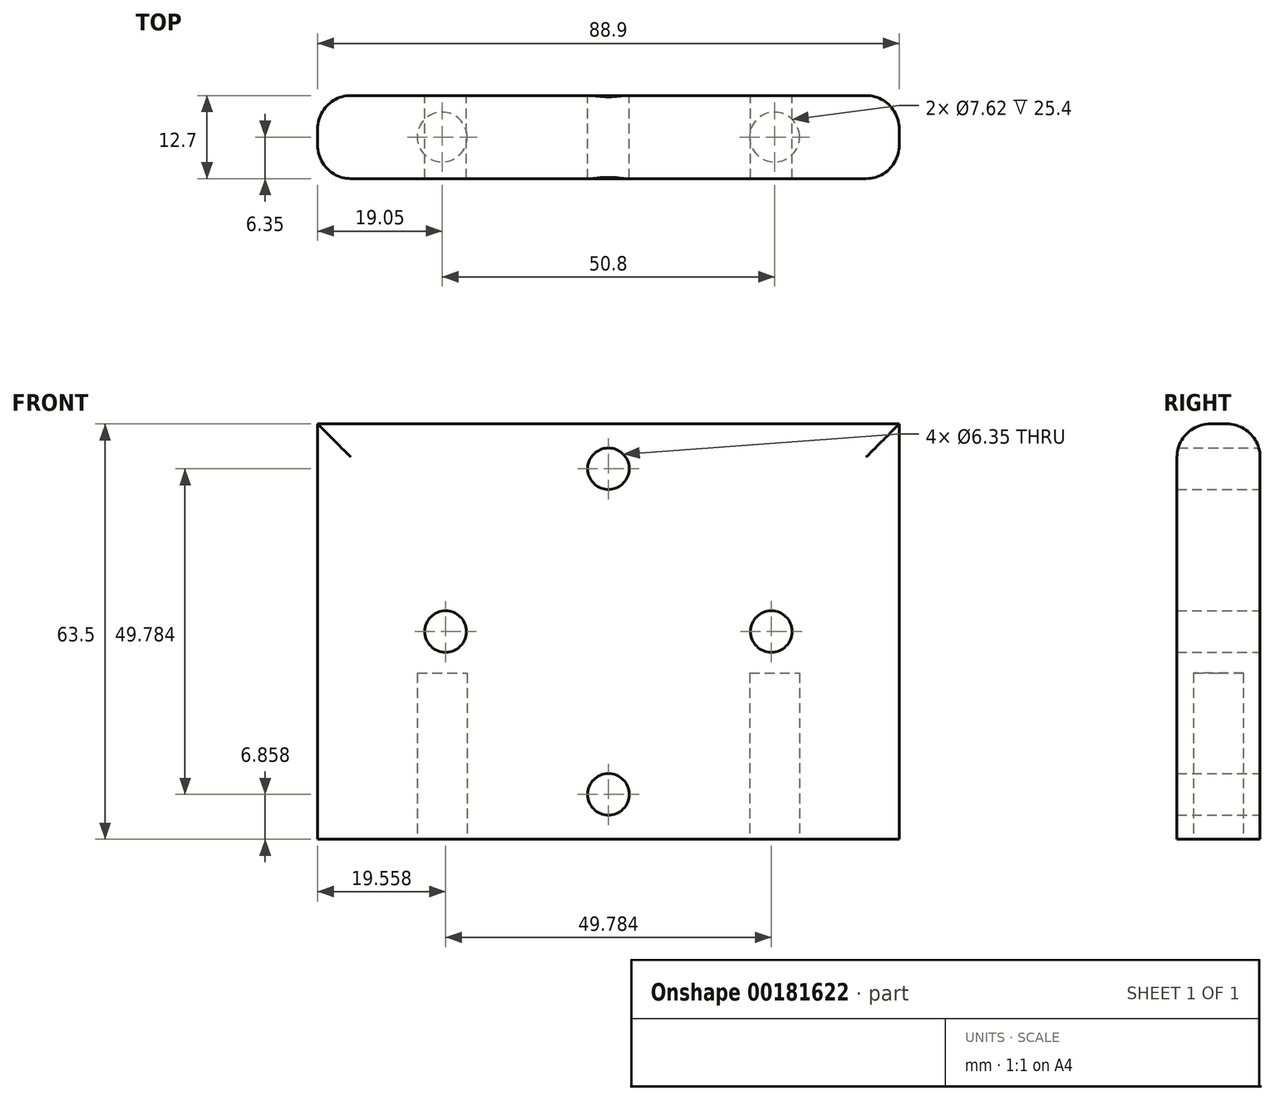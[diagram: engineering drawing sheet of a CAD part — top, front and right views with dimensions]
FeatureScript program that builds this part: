
annotation { "Feature Type Name" : "Feature", "Feature Type Description" : "" }
export const myFeature = defineFeature(function(context is Context, id is Id, definition is map)
    precondition{}
    {
        {
            var Q0;
            Q0=qCreatedBy(makeId("Front.planeOp"),FACE);
            var sketch = newSketch(context, id + "F0", { "sketchPlane" : qUnion([Q0])});
            skLineSegment(sketch, "E0.bottom", {"start": v(44.45, -31.75) * mm, "end": v(-44.45, -31.75) * mm});
            skLineSegment(sketch, "E0.top", {"start": v(44.45, 31.75) * mm, "end": v(-44.45, 31.75) * mm});
            skLineSegment(sketch, "E0.left", {"start": v(44.45, -31.75) * mm, "end": v(44.45, 31.75) * mm});
            skLineSegment(sketch, "E0.right", {"start": v(-44.45, -31.75) * mm, "end": v(-44.45, 31.75) * mm});
            skPoint(sketch, "E0.middle", {"position": v(0, 0) * mm});
            skLineSegment(sketch, "E1", {"start": v(0, 28.07) * mm, "end": v(0, 21.72) * mm});
            skLineSegment(sketch, "E2", {"start": v(-28.07, 0) * mm, "end": v(-21.72, 0) * mm});
            skCircle(sketch, "E3", {"center": v(0, 24.9) * mm, "radius": 3.18 * mm});
            skCircle(sketch, "E4", {"center": v(24.9, 0) * mm, "radius": 3.18 * mm});
            skCircle(sketch, "E5", {"center": v(-24.9, 0) * mm, "radius": 3.18 * mm});
            skCircle(sketch, "E6", {"center": v(0, -24.9) * mm, "radius": 3.18 * mm});
            skPoint(sketch, "E7.orphan", {"position": v(0, 31.75) * mm});
            skPoint(sketch, "E8.orphan", {"position": v(-44.45, 0) * mm});
            skPoint(sketch, "E9.end.orphan", {"position": v(44.45, 0) * mm});
            skPoint(sketch, "E10.start.orphan", {"position": v(0, -31.75) * mm});
            skSolve(sketch);
        }
        {
            var Q0;
            Q0=qSketchRegion(id+"F0",true);
            extrude(context, id + "F1", {"entities" : qUnion([Q0]), "endBound" : BoundingType.SYMMETRIC, "depth" : 12.7 * mm});
        }
        {
            var Q0;
            Q0=makeQuery(id+"F1.opExtrude","SWEPT_FACE",FACE,{"disambiguationData":[OSD([sQuery(id+"F0.wireOp",EDGE,"E0.bottom")])]});
            var sketch = newSketch(context, id + "F2", { "sketchPlane" : qUnion([Q0])});
            skLineSegment(sketch, "E11", {"start": v(0, 0) * mm, "end": v(-25.4, 0) * mm});
            skLineSegment(sketch, "E12", {"start": v(0, 0) * mm, "end": v(25.4, 0) * mm});
            skCircle(sketch, "E13", {"center": v(-25.4, 0) * mm, "radius": 3.81 * mm});
            skCircle(sketch, "E14", {"center": v(25.4, 0) * mm, "radius": 3.81 * mm});
            skSolve(sketch);
        }
        {
            var Q0;
            Q0 = qSketchRegion(id + "F2", true);
            extrude(context, id + "F3", {"entities" : qUnion([Q0]), "operationType" : NewBodyOperationType.REMOVE, "oppositeDirection" : true, "depth" : 25.4 * mm});
        }
        {
            var Q0;
            Q0=makeQuery(id+"F1.opExtrude","CAP_EDGE",EDGE,{"disambiguationData":[OSD([sQuery(id+"F0.wireOp",EDGE,"E0.right")])],"isStart":false});
            var Q1;
            Q1=makeQuery(id+"F1.opExtrude","CAP_EDGE",EDGE,{"disambiguationData":[OSD([sQuery(id+"F0.wireOp",EDGE,"E0.top")])],"isStart":false});
            var Q2;
            Q2=makeQuery(id+"F1.opExtrude","CAP_EDGE",EDGE,{"disambiguationData":[OSD([sQuery(id+"F0.wireOp",EDGE,"E0.left")])],"isStart":false});
            var Q3;
            Q3=makeQuery(id+"F1.opExtrude","CAP_EDGE",EDGE,{"disambiguationData":[OSD([sQuery(id+"F0.wireOp",EDGE,"E0.left")])],"isStart":true});
            var Q4;
            Q4=makeQuery(id+"F1.opExtrude","CAP_EDGE",EDGE,{"disambiguationData":[OSD([sQuery(id+"F0.wireOp",EDGE,"E0.top")])],"isStart":true});
            var Q5;
            Q5=makeQuery(id+"F1.opExtrude","CAP_EDGE",EDGE,{"disambiguationData":[OSD([sQuery(id+"F0.wireOp",EDGE,"E0.right")])],"isStart":true});
            fillet(context, id + "F4", {"entities" : qUnion([Q0, Q1, Q2, Q3, Q4, Q5]), "radius" : 5.08 * mm, "tangentPropagation" : true, "allowEdgeOverflow" : false});
        }
    });
